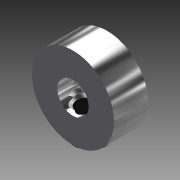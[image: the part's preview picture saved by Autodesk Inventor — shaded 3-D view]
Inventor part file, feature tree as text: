
AUTODESK INVENTOR PART (.ipt)
format: ipt  version: 2012 (Build 160160000, 160)  size: 1,137,664 bytes
history: native  units: in
note: dims shown in document units (in); Inventor stores cm internally (conversion verified against a paired STEP export)
features: other x2, imported_body x2, plane x2, split x2
ambient origin geometry x8: Origin, YZ Plane, XZ Plane, XY Plane, X Axis, Y Axis, Z Axis, Center Point
feature tree (8):
  parser-record x1  (decoder bookkeeping rows leaked as tree rows — omitted from the tree; the rows remain in map.json)
  imported_body  "Base1"
  imported_body  "Base2"
  plane  "Work Plane3"
  plane  "Work Plane4"
  split  "Split1"
  split  "Split2"
  other  "NONE_1"
